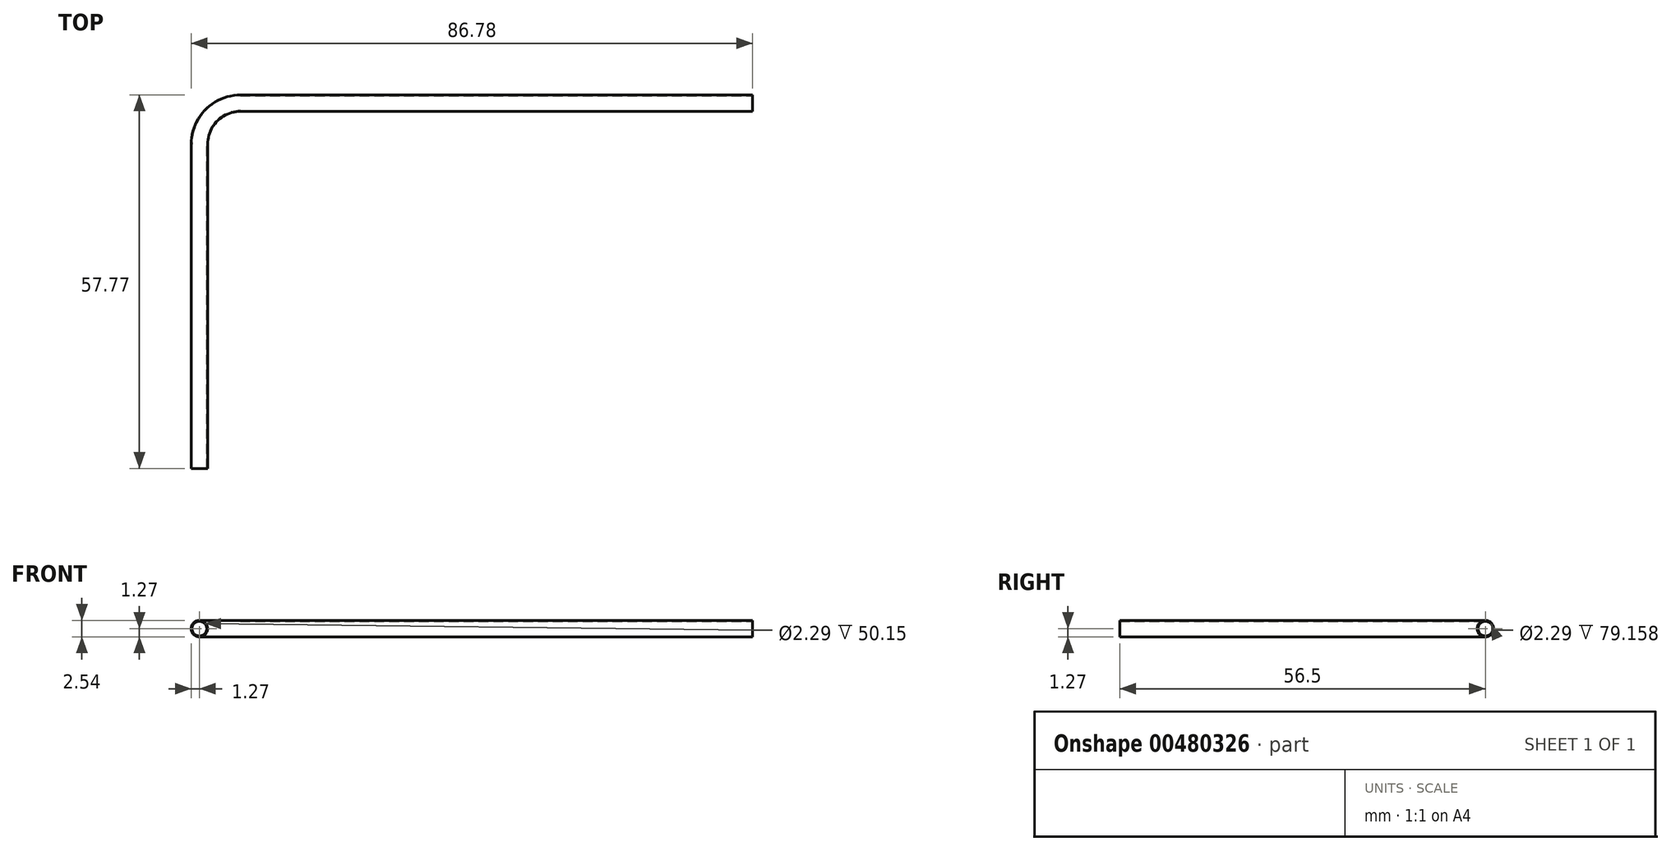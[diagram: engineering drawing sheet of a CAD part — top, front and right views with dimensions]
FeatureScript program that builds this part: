
annotation { "Feature Type Name" : "Feature", "Feature Type Description" : "" }
export const myFeature = defineFeature(function(context is Context, id is Id, definition is map)
    precondition{}
    {
        {
            var Q0;
            Q0=qCreatedBy(makeId("Top.planeOp"),FACE);
            var sketch = newSketch(context, id + "F0", { "sketchPlane" : qUnion([Q0])});
            skLineSegment(sketch, "E0", {"start": v(0, 0) * mm, "end": v(0, 50.15) * mm});
            skLineSegment(sketch, "E1", {"start": v(6.35, 56.5) * mm, "end": v(85.5, 56.5) * mm});
            skPoint(sketch, "E2.visualSharp", {"position": v(0, 56.5) * mm});
            skArc(sketch, "E2.filletArc", {"start": v(6.35, 56.5) * mm, "mid": v(1.86, 54.64) * mm, "end": v(0, 50.15) * mm});
            skSolve(sketch);
        }
        {
            var Q0;
            Q0=qCreatedBy(makeId("Front.planeOp"),FACE);
            var sketch = newSketch(context, id + "F1", { "sketchPlane" : qUnion([Q0])});
            skCircle(sketch, "E3", {"center": v(0, 0) * mm, "radius": 1.27 * mm});
            skCircle(sketch, "E4", {"center": v(0, 0) * mm, "radius": 1.14 * mm});
            skSolve(sketch);
        }
        {
            var Q0;
            Q0=makeQuery(id+"F1.imprint","IMPRINT",FACE,{"disambiguationData":[TD([[makeQuery(id+"F1.imprint","IMPRINT",EDGE,{"derivedFrom":sQuery(id+"F1.wireOp",EDGE,"E3")}),1.0]])]});
            var Q1;
            Q1=sQuery(id+"F0.wireOp",EDGE,"E0");
            var Q2;
            Q2=sQuery(id+"F0.wireOp",EDGE,"E2.filletArc");
            var Q3;
            Q3=sQuery(id+"F0.wireOp",EDGE,"E1");
            sweep(context, id + "F2", {"profiles" : qUnion([Q0]), "path" : qUnion([Q1, Q2, Q3])});
        }
    });
